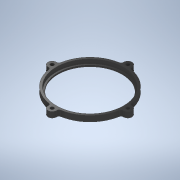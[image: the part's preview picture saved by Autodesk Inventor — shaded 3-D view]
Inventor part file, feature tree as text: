
AUTODESK INVENTOR PART (.ipt)
format: ipt  version: 2020 (Build 240168000, 168)  size: 222,208 bytes
history: native  units: in
note: dims shown in document units (in); Inventor stores cm internally (conversion verified against a paired STEP export)
features: sketch x2, revolve x1, extrude x1, pattern_circular x1, fillet x1
ambient origin geometry x8: Origin, YZ Plane, XZ Plane, XY Plane, X Axis, Y Axis, Z Axis, Center Point
bodies: Solid1 (feature_tree)
feature tree (6):
  revolve  "Revolution1"  [1 undecoded]
  extrude  "Extrusion1"  Depth=0.375in
  pattern_circular  "Circular Pattern1"  Angle=90.0deg  [1 undecoded]
  fillet  "Fillet1"  Radius=0.205in
  sketch  "Sketch1"  dims[d0=2.0in d2=0.25in]
  sketch  "Sketch2"  dims[d3=0.1in d5=0.375in d6=90.0deg d7=0.205in d9=1.0in d10=0.0in d11=1.5748in d12=360.0deg d15=0.0625in d16=2.25in d18=0.5in d19=0.25in d20=2.125in]
note: 2 required parameter values undecoded (feature->parameter linkage not recoverable at this tier; creation-order binding heuristic only, values carry confidence <= 0.55)